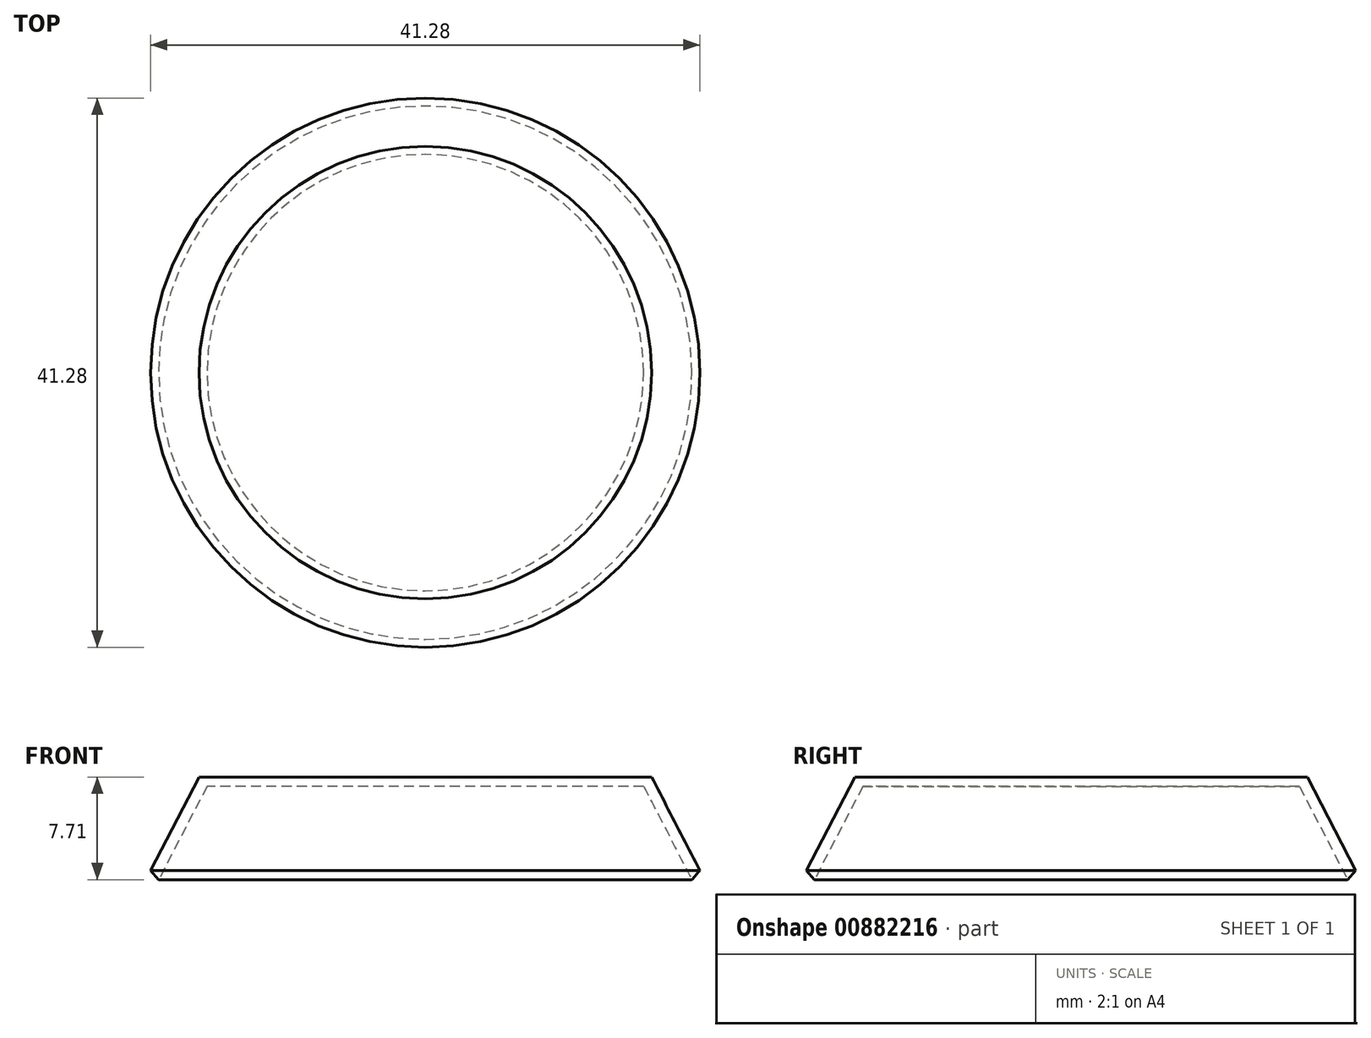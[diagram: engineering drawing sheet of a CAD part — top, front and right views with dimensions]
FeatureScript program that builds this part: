
annotation { "Feature Type Name" : "Feature", "Feature Type Description" : "" }
export const myFeature = defineFeature(function(context is Context, id is Id, definition is map)
    precondition{}
    {
        {
            var Q0;
            Q0=qCreatedBy(makeId("Front.planeOp"),FACE);
            var sketch = newSketch(context, id + "F0", { "sketchPlane" : qUnion([Q0])});
            skLineSegment(sketch, "E0", {"start": v(0, 0) * mm, "end": v(-17, 0) * mm});
            skLineSegment(sketch, "E1", {"start": v(-17, 0) * mm, "end": v(-20.64, -7.01) * mm});
            skLineSegment(sketch, "E2", {"start": v(0.1, -0.7) * mm, "end": v(-16.4, -0.7) * mm});
            skLineSegment(sketch, "E3", {"start": v(-16.4, -0.7) * mm, "end": v(-20.04, -7.71) * mm});
            skLineSegment(sketch, "E4", {"start": v(0, 0) * mm, "end": v(0, -9.67) * mm});
            skLineSegment(sketch, "E5", {"start": v(-20.04, -7.71) * mm, "end": v(-20.64, -7.01) * mm});
            skSolve(sketch);
        }
        {
            var Q0;
            Q0 = qSketchRegion(id + "F0", true);
            var Q1;
            Q1=sQuery(id+"F0.wireOp",EDGE,"E4");
            revolve(context, id + "F1", {"surfaceOperationType" : NewSurfaceOperationType.NEW, "entities" : qUnion([Q0]), "axis" : qUnion([Q1]), "revolveType" : RevolveType.FULL});
        }
    });
